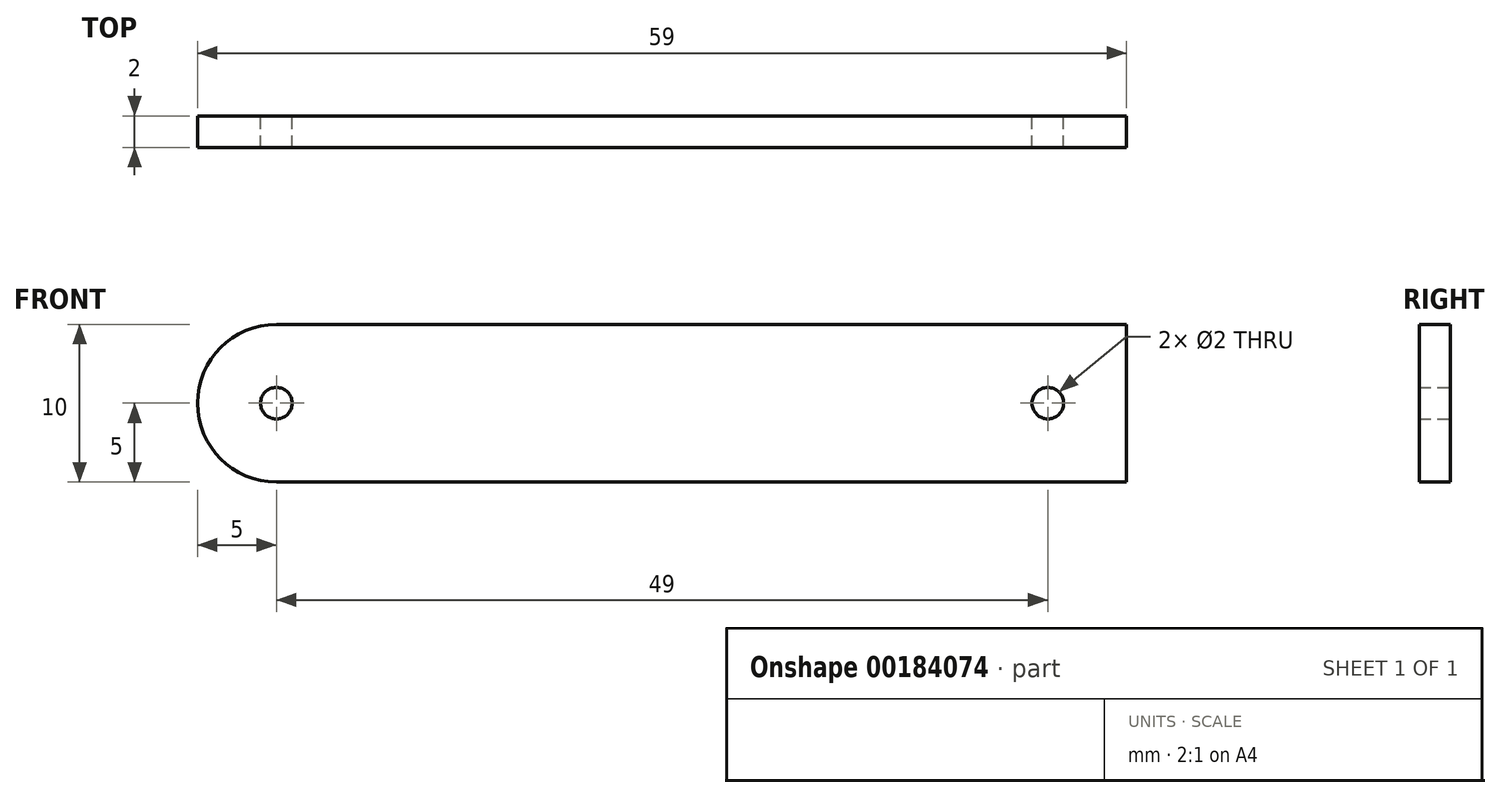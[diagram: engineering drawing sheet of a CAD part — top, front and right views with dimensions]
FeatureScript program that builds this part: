
annotation { "Feature Type Name" : "Feature", "Feature Type Description" : "" }
export const myFeature = defineFeature(function(context is Context, id is Id, definition is map)
    precondition{}
    {
        {
            var Q0;
            Q0=qCreatedBy(makeId("Front.planeOp"),FACE);
            var sketch = newSketch(context, id + "F0", { "sketchPlane" : qUnion([Q0])});
            skLineSegment(sketch, "E0.bottom", {"start": v(0, 0) * mm, "end": v(54, 0) * mm});
            skLineSegment(sketch, "E0.top", {"start": v(0, -10) * mm, "end": v(54, -10) * mm});
            skLineSegment(sketch, "E0.right", {"start": v(54, 0) * mm, "end": v(54, -10) * mm});
            skArc(sketch, "E1", {"start": v(0, 0) * mm, "mid": v(-5, -5) * mm, "end": v(0, -10) * mm});
            skCircle(sketch, "E2", {"center": v(0, -5) * mm, "radius": 1 * mm});
            skCircle(sketch, "E3", {"center": v(49, -5) * mm, "radius": 1 * mm});
            skSolve(sketch);
        }
        {
            var Q0;
            Q0 = qSketchRegion(id + "F0", true);
            extrude(context, id + "F1", {"entities" : qUnion([Q0]), "depth" : 2 * mm});
        }
    });
